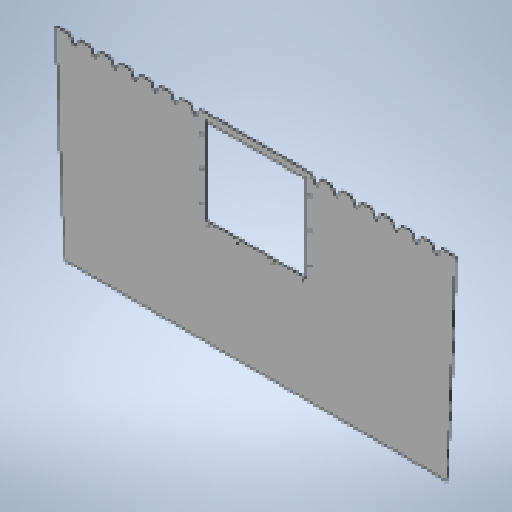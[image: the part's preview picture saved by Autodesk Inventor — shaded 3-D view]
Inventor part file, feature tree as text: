
AUTODESK INVENTOR PART (.ipt)
format: ipt  version: 2025 (Build 290162010, 162A)  size: 338,432 bytes
history: native  units: mm
features: sketch x3, other x2, sheet_metal_op x1, extrude x1, pattern_linear x1, hole x1, mirror x1, projected_geometry x1
ambient origin geometry x8: Origin, YZ Plane, XZ Plane, XY Plane, X Axis, Y Axis, Z Axis, Center Point
bodies: Solid1 (feature_tree)
feature tree (11):
  sheet_metal_op  "Face1"
  extrude  "Extrusion1"  Depth=790.0mm
  pattern_linear  "Rectangular Pattern1"  Count1=20  [1 undecoded]
  sketch  "Sketch7"  dims[d19=370.0mm d23=900.0mm d34=30.0mm d35=5.0mm d36=40.0mm d38=0.0mm d39=0.0mm d40=70.0mm d42=80.0mm d43=30.0mm d44=20.0mm d45=15.0mm d46=240.0mm d47=10.0mm d48=15.0mm d49=190.0mm d50=120.0mm d51=5.1mm d52=6.0mm d53=4.0mm d54=2.0mm d55=90.0deg d56=2.0mm d57=20.594885mm d58=760.0mm d59=790.0mm d60=795.0mm d61=20475.0mm d62=70.0mm]
  hole  "Hole1"  [1 undecoded]
  mirror  "Mirror1"
  sketch  "Sketch1"  dims[d0=513.0mm d2=790.0mm]
  other  "Plate1"
  sketch  "Sketch5"  dims[d3=2.0mm d6=200.0mm]
  projected_geometry  "Projected Loop1"
  other  "Definition1"
note: 2 required parameter values undecoded (feature->parameter linkage not recoverable at this tier; creation-order binding heuristic only, values carry confidence <= 0.55)
